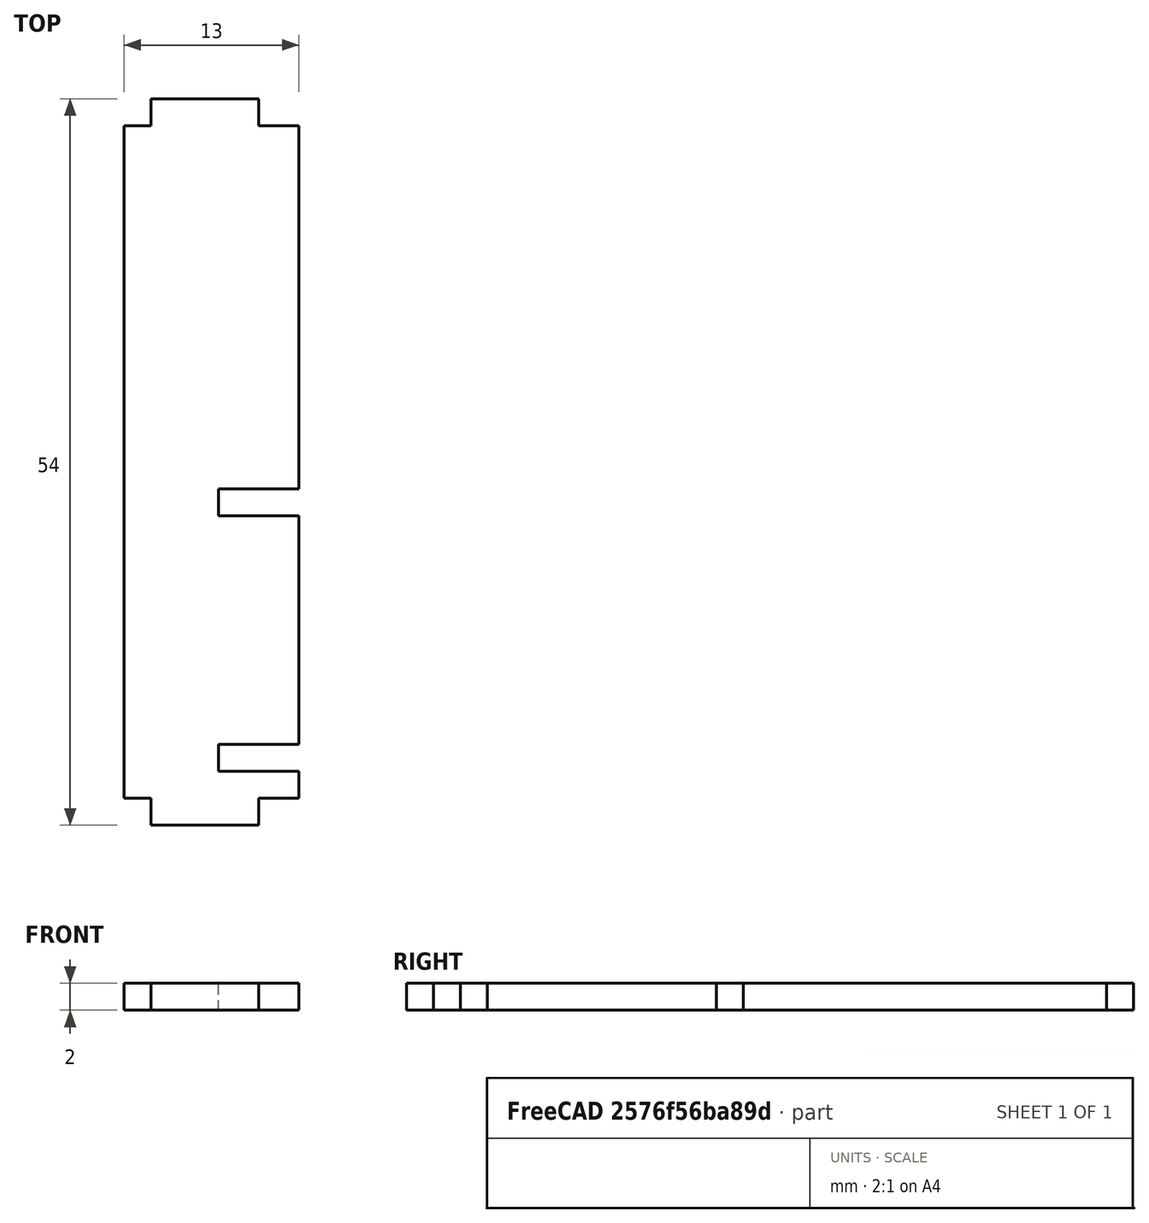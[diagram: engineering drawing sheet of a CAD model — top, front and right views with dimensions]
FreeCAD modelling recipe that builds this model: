
FCSTD DOCUMENT  (FreeCAD 0.18R16131 (Git))
Label: renforts_12
License: All rights reserved
LicenseURL: http://en.wikipedia.org/wiki/All_rights_reserved
objects: Sketcher::SketchObject×1, PartDesign::Pad×1, PartDesign::Body×1
note: 4 computed .brp shape members not serialized (recipe doc carries the construction recipe); baked Part::Feature solids carry a one-line shape summary decoded from their .brp

FEATURE [Sketcher::SketchObject] Sketch
  MapMode = 5
  Support = -> [XY_Plane]
  sketch-geometry (20):
    g0: LineSegment StartX=0 StartY=52 StartZ=0 EndX=2 EndY=52 EndZ=0
    g1: LineSegment StartX=2 StartY=52 StartZ=0 EndX=2 EndY=54 EndZ=0
    g2: LineSegment StartX=2 StartY=54 StartZ=0 EndX=10 EndY=54 EndZ=0
    g3: LineSegment StartX=10 StartY=54 StartZ=0 EndX=10 EndY=52 EndZ=0
    g4: LineSegment StartX=10 StartY=52 StartZ=0 EndX=13 EndY=52 EndZ=0
    g5: LineSegment StartX=13 StartY=52 StartZ=0 EndX=13 EndY=25 EndZ=0
    g6: LineSegment StartX=13 StartY=25 StartZ=0 EndX=7 EndY=25 EndZ=0
    g7: LineSegment StartX=7 StartY=25 StartZ=0 EndX=7 EndY=23 EndZ=0
    g8: LineSegment StartX=7 StartY=23 StartZ=0 EndX=13 EndY=23 EndZ=0
    g9: LineSegment StartX=13 StartY=2 StartZ=0 EndX=10 EndY=2 EndZ=0
    g10: LineSegment StartX=10 StartY=2 StartZ=0 EndX=10 EndY=0 EndZ=0
    g11: LineSegment StartX=10 StartY=0 StartZ=0 EndX=2 EndY=0 EndZ=0
    g12: LineSegment StartX=2 StartY=0 StartZ=0 EndX=2 EndY=2 EndZ=0
    g13: LineSegment StartX=2 StartY=2 StartZ=0 EndX=0 EndY=2 EndZ=0
    g14: LineSegment StartX=0 StartY=2 StartZ=0 EndX=0 EndY=52 EndZ=0
    g15: LineSegment StartX=13 StartY=2 StartZ=0 EndX=13 EndY=4 EndZ=0
    g16: LineSegment StartX=13 StartY=4 StartZ=0 EndX=7 EndY=4 EndZ=0
    g17: LineSegment StartX=7 StartY=4 StartZ=0 EndX=7 EndY=6 EndZ=0
    g18: LineSegment StartX=7 StartY=6 StartZ=0 EndX=13 EndY=6 EndZ=0
    g19: LineSegment StartX=13 StartY=6 StartZ=0 EndX=13 EndY=23 EndZ=0
  constraints (60):
    c: Coincident(g0,g1)
    c: Coincident(g1,g2)
    c: Coincident(g2,g3)
    c: Coincident(g3,g4)
    c: Coincident(g4,g5)
    c: Coincident(g5,g6)
    c: Coincident(g6,g7)
    c: Coincident(g7,g8)
    c: Coincident(g9,g10)
    c: Coincident(g10,g11)
    c: Coincident(g11,g12)
    c: Coincident(g12,g13)
    c: Coincident(g13,g14)
    c: Coincident(g14,g0)
    c: Vertical(g5)
    c: Vertical(g7)
    c: Vertical(g10)
    c: Vertical(g12)
    c: Vertical(g14)
    c: Vertical(g1)
    c: Vertical(g3)
    c: Horizontal(g2)
    c: Horizontal(g0)
    c: Horizontal(g4)
    c: Horizontal(g6)
    c: Horizontal(g8)
    c: Horizontal(g9)
    c: Horizontal(g11)
    c: Horizontal(g13)
    c: PointOnObject(g13,g-2)
    c: PointOnObject(g11,g-1)
    c: Vertical(g8,g5)
    c: DistanceX(g-1,g9) = 13
    c: DistanceX(g6,g6) = 6
    c: DistanceY(g9,g8) = 21
    c: DistanceY(g7,g7) = 2
    c: Equal(g3,g1)
    c: Equal(g1,g7)
    c: Equal(g7,g12)
    c: Vertical(g11,g0)
    c: DistanceX(g13,g13) = 2
    c: DistanceX(g11,g11) = 8
    c: Equal(g11,g2)
    c: Equal(g12,g10)
    c: DistanceY(g14,g14) = 50
    c: Coincident(g15,g16)
    c: Coincident(g16,g17)
    c: Coincident(g17,g18)
    c: Coincident(g18,g19)
    c: Coincident(g19,g8)
    c: Coincident(g9,g15)
    c: Vertical(g19)
    c: Vertical(g15)
    c: Vertical(g17)
    c: Horizontal(g18)
    c: Horizontal(g16)
    c: Equal(g7,g17)
    c: DistanceY(g15,g15) = 2
    c: Equal(g18,g8)
    c: Vertical(g18,g15)
FEATURE [PartDesign::Pad] Pad
  Length = 2
  Length2 = 100
  Profile = -> Sketch
  Type = 0
FEATURE [PartDesign::Body] Body
  Group = -> [Sketch,Pad]
  Origin = -> Origin
  Tip = -> Pad
